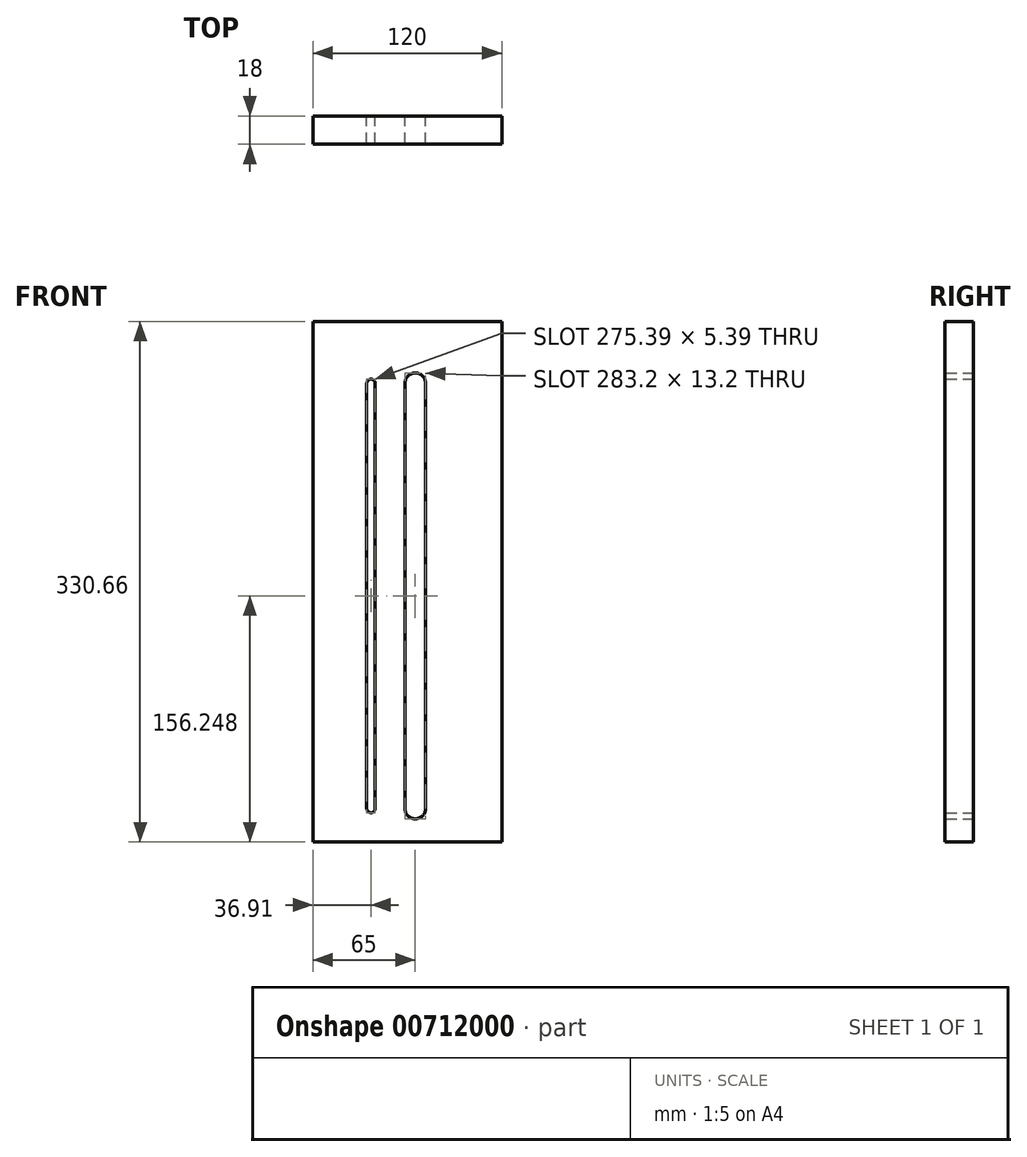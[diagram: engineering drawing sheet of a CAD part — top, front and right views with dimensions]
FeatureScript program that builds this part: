
annotation { "Feature Type Name" : "Feature", "Feature Type Description" : "" }
export const myFeature = defineFeature(function(context is Context, id is Id, definition is map)
    precondition{}
    {
        {
            var Q0;
            Q0=qCreatedBy(makeId("Front.planeOp"),FACE);
            var sketch = newSketch(context, id + "F0", { "sketchPlane" : qUnion([Q0])});
            skLineSegment(sketch, "E0.bottom", {"start": v(60, -165.33) * mm, "end": v(-60, -165.33) * mm});
            skLineSegment(sketch, "E0.top", {"start": v(60, 165.33) * mm, "end": v(-60, 165.33) * mm});
            skLineSegment(sketch, "E0.left", {"start": v(60, -165.33) * mm, "end": v(60, 165.33) * mm});
            skLineSegment(sketch, "E0.right", {"start": v(-60, -165.33) * mm, "end": v(-60, 165.33) * mm});
            skPoint(sketch, "E0.middle", {"position": v(0, 0) * mm});
            skArc(sketch, "E1", {"start": v(11.6, 125.92) * mm, "mid": v(5, 132.52) * mm, "end": v(-1.6, 125.92) * mm});
            skArc(sketch, "E2", {"start": v(-20.4, 125.92) * mm, "mid": v(-23.1, 128.61) * mm, "end": v(-25.79, 125.92) * mm});
            skArc(sketch, "E3", {"start": v(-1.6, -144.08) * mm, "mid": v(5, -150.68) * mm, "end": v(11.6, -144.08) * mm});
            skArc(sketch, "E4", {"start": v(-25.79, -144.08) * mm, "mid": v(-23.1, -146.78) * mm, "end": v(-20.4, -144.08) * mm});
            skLineSegment(sketch, "E5", {"start": v(-25.79, -144.08) * mm, "end": v(-25.79, 125.92) * mm});
            skLineSegment(sketch, "E6", {"start": v(-20.4, 125.92) * mm, "end": v(-20.4, -144.08) * mm});
            skLineSegment(sketch, "E7", {"start": v(11.6, 125.92) * mm, "end": v(11.6, -144.08) * mm});
            skLineSegment(sketch, "E8", {"start": v(-1.6, 125.92) * mm, "end": v(-1.6, -144.08) * mm});
            skSolve(sketch);
        }
        {
            var Q0;
            Q0 = qSketchRegion(id + "F0", true);
            extrude(context, id + "F1", {"entities" : qUnion([Q0]), "depth" : 18 * mm, "offsetDistance" : 25 * mm});
        }
    });
